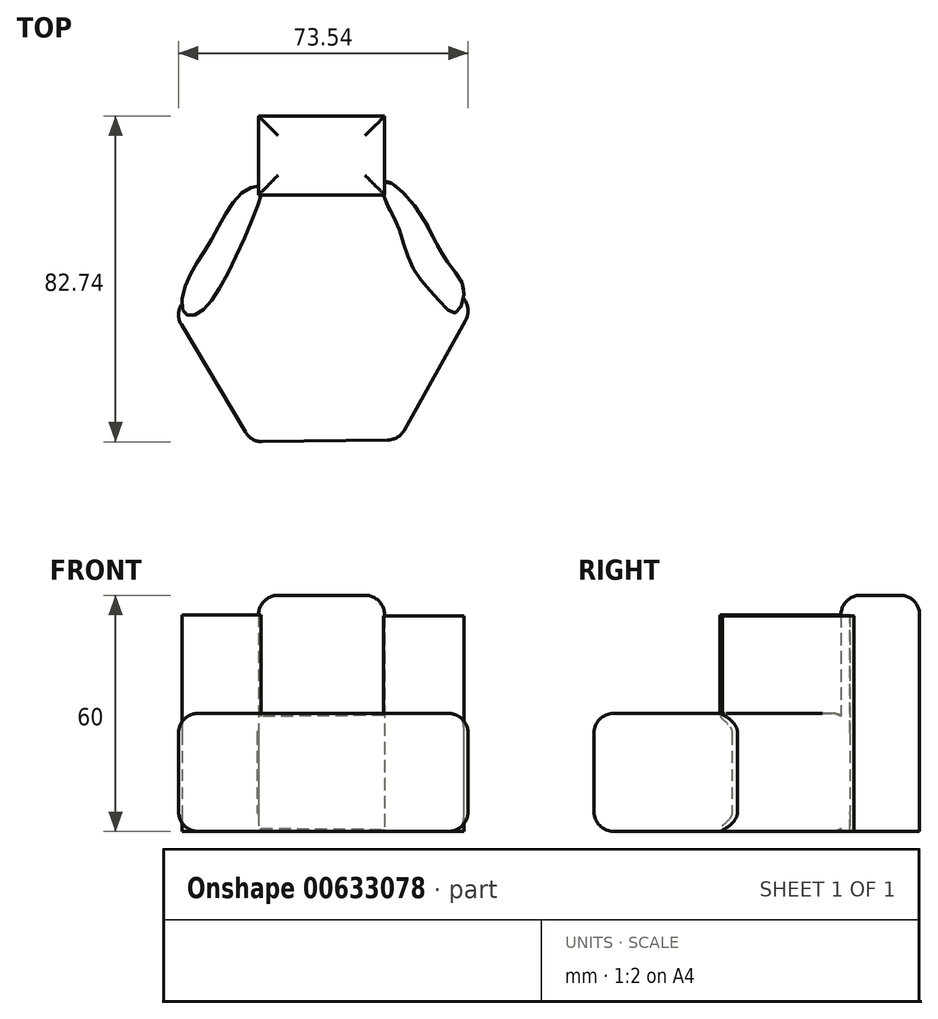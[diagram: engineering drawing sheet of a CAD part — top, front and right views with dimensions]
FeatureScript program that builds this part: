
annotation { "Feature Type Name" : "Feature", "Feature Type Description" : "" }
export const myFeature = defineFeature(function(context is Context, id is Id, definition is map)
    precondition{}
    {
        {
            var Q0;
            Q0=qCreatedBy(makeId("Top.planeOp"),FACE);
            var sketch = newSketch(context, id + "F0", { "sketchPlane" : qUnion([Q0])});
            skCircle(sketch, "E0.cCircle", {"center": v(0, 0) * mm, "radius": 32.52 * mm, "construction": true});
            skLineSegment(sketch, "E0.0", {"start": v(-37.55, -0.52) * mm, "end": v(-19.23, 32.26) * mm});
            skLineSegment(sketch, "E0.1", {"start": v(-19.23, 32.26) * mm, "end": v(18.32, 32.78) * mm});
            skLineSegment(sketch, "E0.2", {"start": v(18.32, 32.78) * mm, "end": v(37.55, 0.52) * mm});
            skLineSegment(sketch, "E0.3", {"start": v(37.55, 0.52) * mm, "end": v(19.23, -32.26) * mm});
            skLineSegment(sketch, "E0.4", {"start": v(19.23, -32.26) * mm, "end": v(-18.32, -32.78) * mm});
            skLineSegment(sketch, "E0.5", {"start": v(-18.32, -32.78) * mm, "end": v(-37.55, -0.52) * mm});
            skPoint(sketch, "E0.0.midPoint", {"position": v(-28.39, 15.87) * mm});
            skSolve(sketch);
        }
        {
            var Q0;
            Q0=makeQuery(id+"F0.imprint","IMPRINT",FACE,{"disambiguationData":[TD([[makeQuery(id+"F0.imprint","IMPRINT",EDGE,{"derivedFrom":sQuery(id+"F0.wireOp",EDGE,"E0.0")}),-1.0]])]});
            extrude(context, id + "F1", {"entities" : qUnion([Q0]), "depth" : 30 * mm, "offsetDistance" : 25 * mm});
        }
        {
            var Q0;
            Q0=makeQuery(id+"F1.opExtrude","SWEPT_FACE",FACE,{"disambiguationData":[OSD([sQuery(id+"F0.wireOp",EDGE,"E0.4")])]});
            var Q1;
            Q1=makeQuery(id+"F1.opExtrude","SWEPT_FACE",FACE,{"disambiguationData":[OSD([sQuery(id+"F0.wireOp",EDGE,"E0.5")])]});
            var Q2;
            Q2=makeQuery(id+"F1.opExtrude","SWEPT_FACE",FACE,{"disambiguationData":[OSD([sQuery(id+"F0.wireOp",EDGE,"E0.3")])]});
            var Q3;
            Q3=makeQuery(id+"F1.opExtrude","CAP_FACE",FACE,{"disambiguationData":[OSD([sQuery(id+"F0.wireOp",EDGE,"E0.0"),sQuery(id+"F0.wireOp",EDGE,"E0.1"),sQuery(id+"F0.wireOp",EDGE,"E0.2"),sQuery(id+"F0.wireOp",EDGE,"E0.3"),sQuery(id+"F0.wireOp",EDGE,"E0.4"),sQuery(id+"F0.wireOp",EDGE,"E0.5")])],"isStart":false});
            var Q4;
            Q4=makeQuery(id+"F1.opExtrude","SWEPT_FACE",FACE,{"disambiguationData":[OSD([sQuery(id+"F0.wireOp",EDGE,"E0.2")])]});
            var Q5;
            Q5=makeQuery(id+"F1.opExtrude","SWEPT_FACE",FACE,{"disambiguationData":[OSD([sQuery(id+"F0.wireOp",EDGE,"E0.1")])]});
            var Q6;
            Q6=makeQuery(id+"F1.opExtrude","CAP_FACE",FACE,{"disambiguationData":[OSD([sQuery(id+"F0.wireOp",EDGE,"E0.0"),sQuery(id+"F0.wireOp",EDGE,"E0.1"),sQuery(id+"F0.wireOp",EDGE,"E0.2"),sQuery(id+"F0.wireOp",EDGE,"E0.3"),sQuery(id+"F0.wireOp",EDGE,"E0.4"),sQuery(id+"F0.wireOp",EDGE,"E0.5")])],"isStart":true});
            var Q7;
            Q7=makeQuery(id+"F1.opExtrude","SWEPT_FACE",FACE,{"disambiguationData":[OSD([sQuery(id+"F0.wireOp",EDGE,"E0.0")])]});
            fillet(context, id + "F2", {"entities" : qUnion([Q0, Q1, Q2, Q3, Q4, Q5, Q6, Q7]), "radius" : 5 * mm, "tangentPropagation" : true, "allowEdgeOverflow" : false});
        }
        {
            var Q0;
            Q0=qCreatedBy(makeId("Front.planeOp"),FACE);
            cPlane(context, id + "F3", {"entities" : qUnion([Q0]), "cplaneType" : CPlaneType.OFFSET, "offset" : 30 * mm, "oppositeDirection" : true, "width" : 150 * mm, "height" : 150 * mm});
        }
        {
            var Q0;
            Q0=qCreatedBy(id+"F3.planeOp",FACE);
            var sketch = newSketch(context, id + "F4", { "sketchPlane" : qUnion([Q0])});
            skLineSegment(sketch, "E1.bottom", {"start": v(15.58, 60) * mm, "end": v(-16.45, 60) * mm});
            skLineSegment(sketch, "E1.top", {"start": v(15.58, 0) * mm, "end": v(-16.45, 0) * mm});
            skLineSegment(sketch, "E1.left", {"start": v(15.58, 60) * mm, "end": v(15.58, 0) * mm});
            skLineSegment(sketch, "E1.right", {"start": v(-16.45, 60) * mm, "end": v(-16.45, 0) * mm});
            skSolve(sketch);
        }
        {
            var Q0;
            Q0 = qSketchRegion(id + "F4", true);
            extrude(context, id + "F5", {"entities" : qUnion([Q0]), "operationType" : NewBodyOperationType.ADD, "oppositeDirection" : true, "depth" : 20 * mm, "offsetDistance" : 25 * mm});
        }
        {
            var Q0;
            Q0=makeQuery(id+"F5.opExtrude","SWEPT_EDGE",EDGE,{"disambiguationData":[OSD([sQuery(id+"F4.wireOp",EDGE,"E1.bottom"),sQuery(id+"F4.wireOp",EDGE,"E1.left")])]});
            var Q1;
            Q1=makeQuery(id+"F5.opExtrude","CAP_EDGE",EDGE,{"disambiguationData":[OSD([sQuery(id+"F4.wireOp",EDGE,"E1.bottom")])],"isStart":true});
            var Q2;
            Q2=makeQuery(id+"F5.opExtrude","SWEPT_EDGE",EDGE,{"disambiguationData":[OSD([sQuery(id+"F4.wireOp",EDGE,"E1.bottom"),sQuery(id+"F4.wireOp",EDGE,"E1.right")])]});
            var Q3;
            Q3=makeQuery(id+"F5.opExtrude","CAP_EDGE",EDGE,{"disambiguationData":[OSD([sQuery(id+"F4.wireOp",EDGE,"E1.bottom")])],"isStart":false});
            fillet(context, id + "F6", {"entities" : qUnion([Q0, Q1, Q2, Q3]), "radius" : 5 * mm, "tangentPropagation" : true, "allowEdgeOverflow" : false});
        }
        {
            var Q0;
            Q0=qCreatedBy(makeId("Top.planeOp"),FACE);
            var sketch = newSketch(context, id + "F7", { "sketchPlane" : qUnion([Q0])});
            skFitSpline(sketch, "E2", {"points": [v(15.28, 30.13) * mm, v(15.87, 33.34) * mm, v(24.02, 26.06) * mm, v(31.3, 13.25) * mm, v(35.66, 5.97) * mm, v(33.63, 0) * mm, v(28.97, 3.64) * mm, v(22.56, 11.8) * mm, v(19.07, 21.69) * mm, v(15.28, 30.13) * mm]});
            skSolve(sketch);
        }
        {
            var Q0;
            Q0 = qSketchRegion(id + "F7", true);
            extrude(context, id + "F8", {"entities" : qUnion([Q0]), "operationType" : NewBodyOperationType.ADD, "depth" : 54.8 * mm, "offsetDistance" : 25 * mm});
        }
        {
            var Q0;
            Q0=qCreatedBy(makeId("Top.planeOp"),FACE);
            var sketch = newSketch(context, id + "F9", { "sketchPlane" : qUnion([Q0])});
            skFitSpline(sketch, "E3", {"points": [v(-15.87, 29.84) * mm, v(-16.16, 32.17) * mm, v(-21.1, 30.13) * mm, v(-28.1, 19.07) * mm, v(-34.5, 8.3) * mm, v(-35.37, 0) * mm, v(-31.59, 0) * mm, v(-23.44, 11.8) * mm, v(-15.87, 29.84) * mm]});
            skSolve(sketch);
        }
        {
            var Q0;
            Q0 = qSketchRegion(id + "F9", true);
            extrude(context, id + "F10", {"entities" : qUnion([Q0]), "operationType" : NewBodyOperationType.ADD, "depth" : 55 * mm, "offsetDistance" : 25 * mm});
        }
    });
